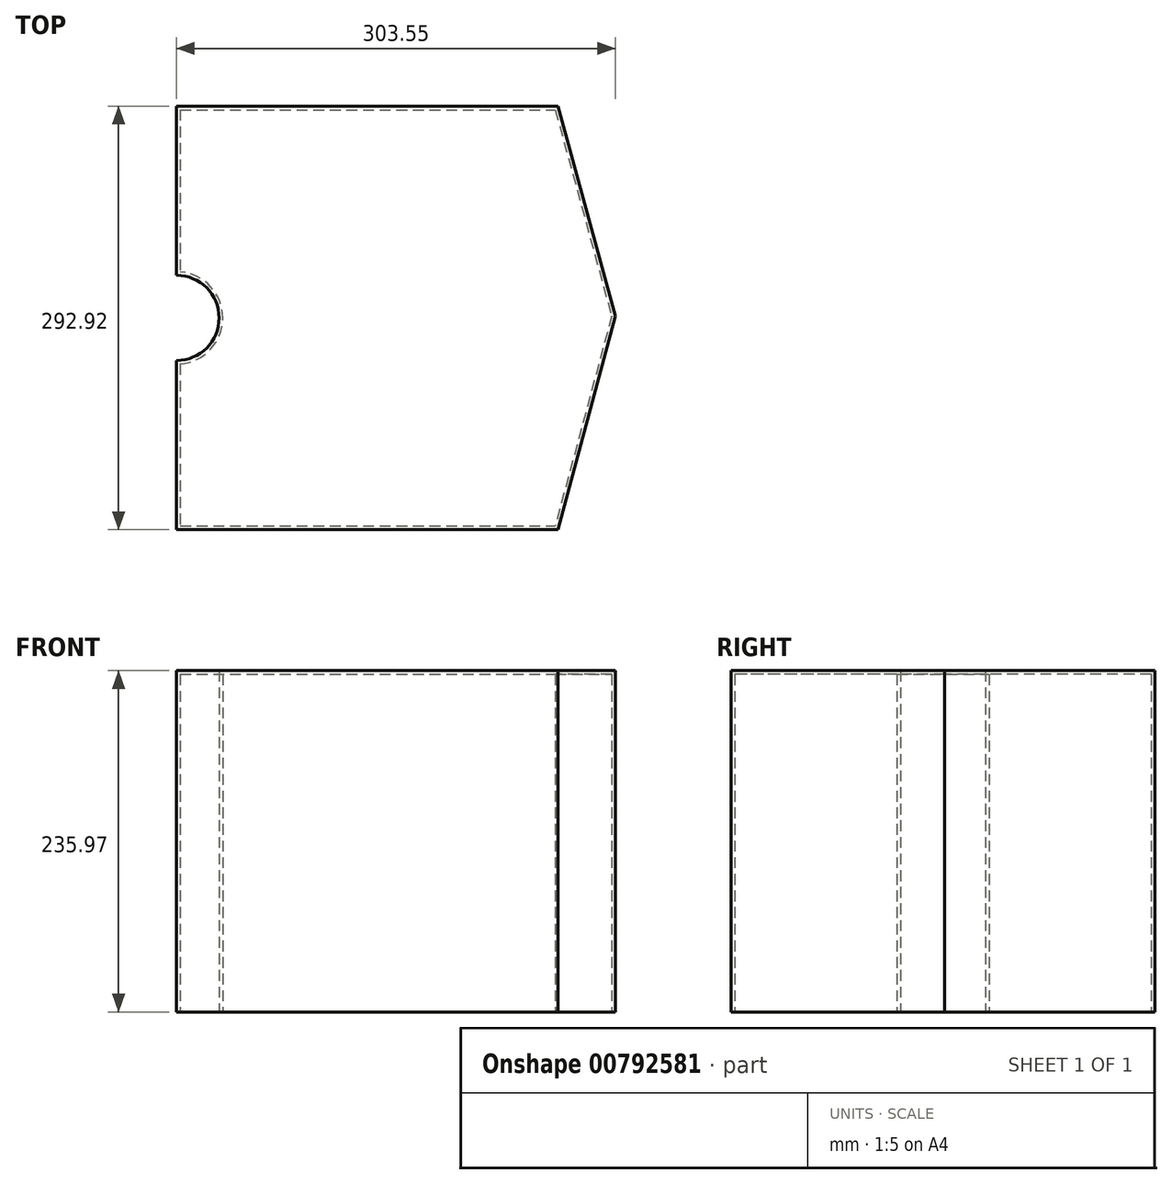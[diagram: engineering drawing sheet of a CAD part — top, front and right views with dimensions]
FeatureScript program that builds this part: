
annotation { "Feature Type Name" : "Feature", "Feature Type Description" : "" }
export const myFeature = defineFeature(function(context is Context, id is Id, definition is map)
    precondition{}
    {
        {
            var Q0;
            Q0=qCreatedBy(makeId("Top.planeOp"),FACE);
            var sketch = newSketch(context, id + "F0", { "sketchPlane" : qUnion([Q0])});
            skLineSegment(sketch, "E0.bottom", {"start": v(-310.68, 114.65) * mm, "end": v(-46.83, 114.65) * mm});
            skLineSegment(sketch, "E0.top", {"start": v(-310.68, -178.27) * mm, "end": v(-46.83, -178.27) * mm});
            skLineSegment(sketch, "E0.left", {"start": v(-310.68, 114.65) * mm, "end": v(-310.68, -178.27) * mm});
            skLineSegment(sketch, "E0.right", {"start": v(-46.83, 114.65) * mm, "end": v(-46.83, -178.27) * mm});
            skCircle(sketch, "E1", {"center": v(-310.68, -31.81) * mm, "radius": 29.43 * mm});
            skLineSegment(sketch, "E2", {"start": v(-46.83, 114.65) * mm, "end": v(-7.13, -30.58) * mm});
            skLineSegment(sketch, "E3", {"start": v(-7.13, -30.58) * mm, "end": v(-46.83, -178.27) * mm});
            skLineSegment(sketch, "E4", {"start": v(-310.68, 114.65) * mm, "end": v(-46.83, -178.27) * mm});
            skSolve(sketch);
        }
        {
            var Q0;
            Q0=makeQuery(id+"F0.imprint","IMPRINT",FACE,{"disambiguationData":[TD([[makeQuery(id+"F0.imprint","IMPRINT",EDGE,{"derivedFrom":sQuery(id+"F0.wireOp",EDGE,"E0.bottom")}),-1.0]])]});
            var Q1;
            {var subQ1=sQuery(id+"F0.wireOp",EDGE,"E0.top");Q1=makeQuery(id+"F0.imprint","IMPRINT",FACE,{"disambiguationData":[TD([[makeQuery(id+"F0.imprint","IMPRINT",EDGE,{"derivedFrom":subQ1}),1.0]])]});}
            var Q2;
            Q2=makeQuery(id+"F0.imprint","IMPRINT",FACE,{"disambiguationData":[TD([[makeQuery(id+"F0.imprint","IMPRINT",EDGE,{"derivedFrom":sQuery(id+"F0.wireOp",EDGE,"E0.right")}),1.0]])]});
            extrude(context, id + "F1", {"entities" : qUnion([Q0, Q1, Q2]), "depth" : 235.97 * mm, "offsetDistance" : 25.4 * mm});
        }
        {
            var Q0;
            Q0=makeQuery(id+"F1.opExtrude","CAP_FACE",FACE,{"disambiguationData":[OSD([sQuery(id+"F0.wireOp",EDGE,"E0.bottom"),sQuery(id+"F0.wireOp",EDGE,"E0.top"),sQuery(id+"F0.wireOp",EDGE,"E0.left"),sQuery(id+"F0.wireOp",EDGE,"E1"),sQuery(id+"F0.wireOp",EDGE,"E2"),sQuery(id+"F0.wireOp",EDGE,"E3")])],"isStart":true});
            shell(context, id + "F2", {"entities" : qUnion([Q0]), "thickness" : 2.54 * mm});
        }
    });
